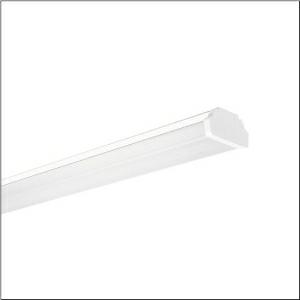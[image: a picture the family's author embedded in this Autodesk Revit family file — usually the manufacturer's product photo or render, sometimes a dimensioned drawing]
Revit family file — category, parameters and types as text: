
# Revit family: dus_r__31_gen_2_53bd812cv685c2_c333
name_source: partatom
category: Lighting Fixtures
units: mm (PartAtom-declared; Revit-internal decimal feet)

## family parameters
Cut with Voids When Loaded = No
Host = Face
Light Source = No
Part Type = Normal
Room Calculation Point = No
Round Connector Dimension = Use Diameter
Shared = No

## types (1)
- --- (1 x LED, 8970 lm, 49.9 W, 6500K)
    Apparent Load = 50 VA
    CIE Flux Codes = 47 80 95 93 100
    Color Rendering = 80
    Color Temperature = 6500K
    Default Elevation = 1800 mm
    Description = DUS® 31 Gen.2, luminaire insert, of sheet steel, coil coated, white, length: 1.535mm, width: 81mm, height: 90mm, 5x system unit, system units: 307mm, LED rated luminous flux: 8.970lm, light colour: 865, control gear: ON/OFF Multilumen, CLOi, with plug, 3-pole, with phase selection, mains connection: 220..240V, AC, 50/60Hz, start of lifetime: 50W, end of service life: 61W, through-wiring accessed according to module size, primary optical cover: cover, of PMMA, light emission: direct distribution, primary light characteristic: symmetric, protection rating (complete): IP20, protection rating (LED compartment): IP50, insulation class (complete): insulation class I (protective earthing), certification: CE, ENEC, VDE, UKCA, impact resistance: IK03, permissible ambient temperature for indoor applications: -35..+40°C, corresponds to IFS (International Featured Standards) requirements for safety and quality in the food industry, reducing of maximum allowable ambient temperature of 5°C with ceiling mounting, packaging unit: 1 piece
    Height = 95 mm
    Lamp = 1 x LED
    Lamp Light Flux = 8970 lm
    Lamp Power = 49.9 W
    Lamp count = 1
    Length = 1535 mm
    Luminous efficacy = 180 lm/W
    Manufacturer = Siteco
    ModVariant = No
    Model = 53BD812CV685C2
    Mounting Place = Ceiling
    Mounting Type = Pendant
    Number of Poles = 1
    OnlyDefault = Yes
    Power Factor = 1
    Product Name = DUS® 31 Gen.2
    Product group = luminaire insert | ceiling pendant
    ProductGroupID = 902
    Protection Class = Protection class I
    Protection Degree = IP 20
    RLX_Detail_Level = 1
    RLX_Emergency_Light_Flux = 0 lm
    RLX_Emergency_Type = 0
    RLX_Emergency_Type_DB = No
    RlxData = <blob elided: 29781 chars, md5=bba071ca>
    Socket = socket
    Standby Power = 0 W
    System Light Flux = 8970 lm
    System Power = 50 W
    Type Comments = factory setting: luminous flux: 100 % | (A | C | E) | 116 mA
    Type Image = l_1319596.jpg
    URL = http://relux.com
    VarID = @adj_063073
    Voltage = 0 V
    Weight = 0.00 kg
    Width = 81 mm

## geometry (parser evidence)
native form markers: Blend x4, Sweep x12
no freeform markers — native parametric forms only
